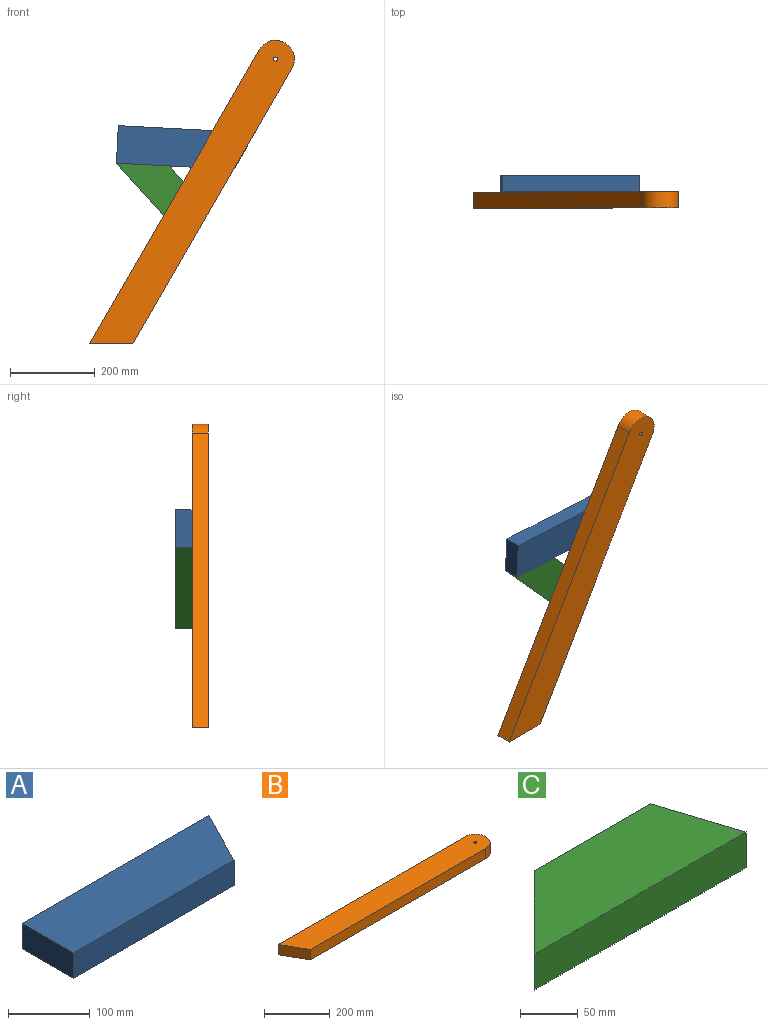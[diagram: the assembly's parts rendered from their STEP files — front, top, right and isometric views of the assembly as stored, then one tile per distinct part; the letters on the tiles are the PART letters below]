
ASSEMBLY  parts=3 mates=2
PART A: 6 faces, bbox 323.9x88.9x38.1 mm
  f0: plane 88.9x45.3mm, normal (0.89,-0.45,0), area 3801.4mm2, adj f1,f3,f4,f5
  f1: plane 323.85x38.1mm, normal (0,1,0), area 12338.7mm2, adj f0,f2,f4,f5
  f2: plane 88.9x38.1mm, normal (-1,0,0), area 3387.1mm2, adj f1,f3,f4,f5
  f3: plane 278.55x38.1mm, normal (0,-1,0), area 10612.9mm2, adj f0,f2,f4,f5
  f4: plane 323.85x88.9mm, normal (0,0,1), area 26776.8mm2, adj f0,f1,f2,f3
  f5: plane 323.85x88.9mm, normal (0,0,-1), area 26776.8mm2, adj f0,f1,f2,f3
PART B: 7 faces, bbox 847.7x88.9x38.1 mm
  f0: plane 751.95x38.1mm, normal (0,-1,0), area 28649.2mm2, adj f1,f4,f5,f6
  f1: cylinder r=44.45mm len=88.9mm, axis (0,0,-1), area 5320.4mm2, adj f0,f2,f5,f6
  f2: plane 803.28x38.1mm, normal (0,1,0), area 30604.8mm2, adj f1,f4,f5,f6
  f3: cylinder r=4.76mm len=38.1mm, axis (0,0,-1), area 1140.1mm2, adj f5,f6
  f4: plane 88.9x51.33mm, normal (-0.87,-0.5,0), area 3911.1mm2, adj f0,f2,f5,f6
  f5: plane 847.73x88.9mm, normal (0,0,1), area 72162mm2, adj f0,f1,f2,f3,f4
  f6: plane 847.73x88.9mm, normal (0,0,-1), area 72162mm2, adj f0,f1,f2,f3,f4
PART C: 6 faces, bbox 260.4x88.9x38.1 mm
  f0: plane 88.9x88.9mm, normal (-0.71,0.71,0), area 4790.1mm2, adj f1,f3,f4,f5
  f1: plane 260.35x38.1mm, normal (0,-1,0), area 9919.3mm2, adj f0,f2,f4,f5
  f2: plane 88.9x38.1mm, normal (0.95,0.31,0), area 3561.4mm2, adj f1,f3,f4,f5
  f3: plane 142.56x38.1mm, normal (0,1,0), area 5431.7mm2, adj f0,f2,f4,f5
  f4: plane 260.35x88.9mm, normal (0,0,1), area 17909.6mm2, adj f0,f1,f2,f3
  f5: plane 260.35x88.9mm, normal (0,0,-1), area 17909.6mm2, adj f0,f1,f2,f3
PLACE A rot(axis=(1,0.03,-0.03),90deg) t=(178.37,57.15,507.43)mm
PLACE B rot(axis=(0.77,-0.45,0.45),104.5deg) t=(187.99,19.05,325.6)mm fixed
PLACE C rot(axis=(0.85,0.38,-0.38),99.5deg) t=(99.12,57.15,330.39)mm
MATE fastened B.f0 <-> C.f2  axis (0.87,0,-0.5) through (239.31,19.05,325.6)mm
MATE fastened C.f0 <-> A.f3  axis (0.05,0,1) through (12.02,57.15,427.13)mm
